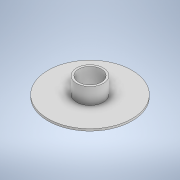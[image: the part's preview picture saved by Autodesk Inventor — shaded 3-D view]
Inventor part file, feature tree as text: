
AUTODESK INVENTOR PART (.ipt)
format: ipt  version: 2021 (Build 250183000, 183)  size: 120,320 bytes
history: native  units: mm
features: revolve x1, sketch x1
ambient origin geometry x8: Origin, YZ Plane, XZ Plane, XY Plane, X Axis, Y Axis, Z Axis, Center Point
bodies: Solid1 (feature_tree)
feature tree (2):
  revolve  "Revolution1"  [1 undecoded]
  sketch  "Sketch1"  dims[d0=4.0mm d1=8.0mm d2=0.0mm d3=2.5mm d4=3.0mm d7=2.5mm d8=35.0mm d9=13.95mm d10=20.0mm d11=90.0deg]
note: 1 required parameter value undecoded (feature->parameter linkage not recoverable at this tier; creation-order binding heuristic only, values carry confidence <= 0.55)
